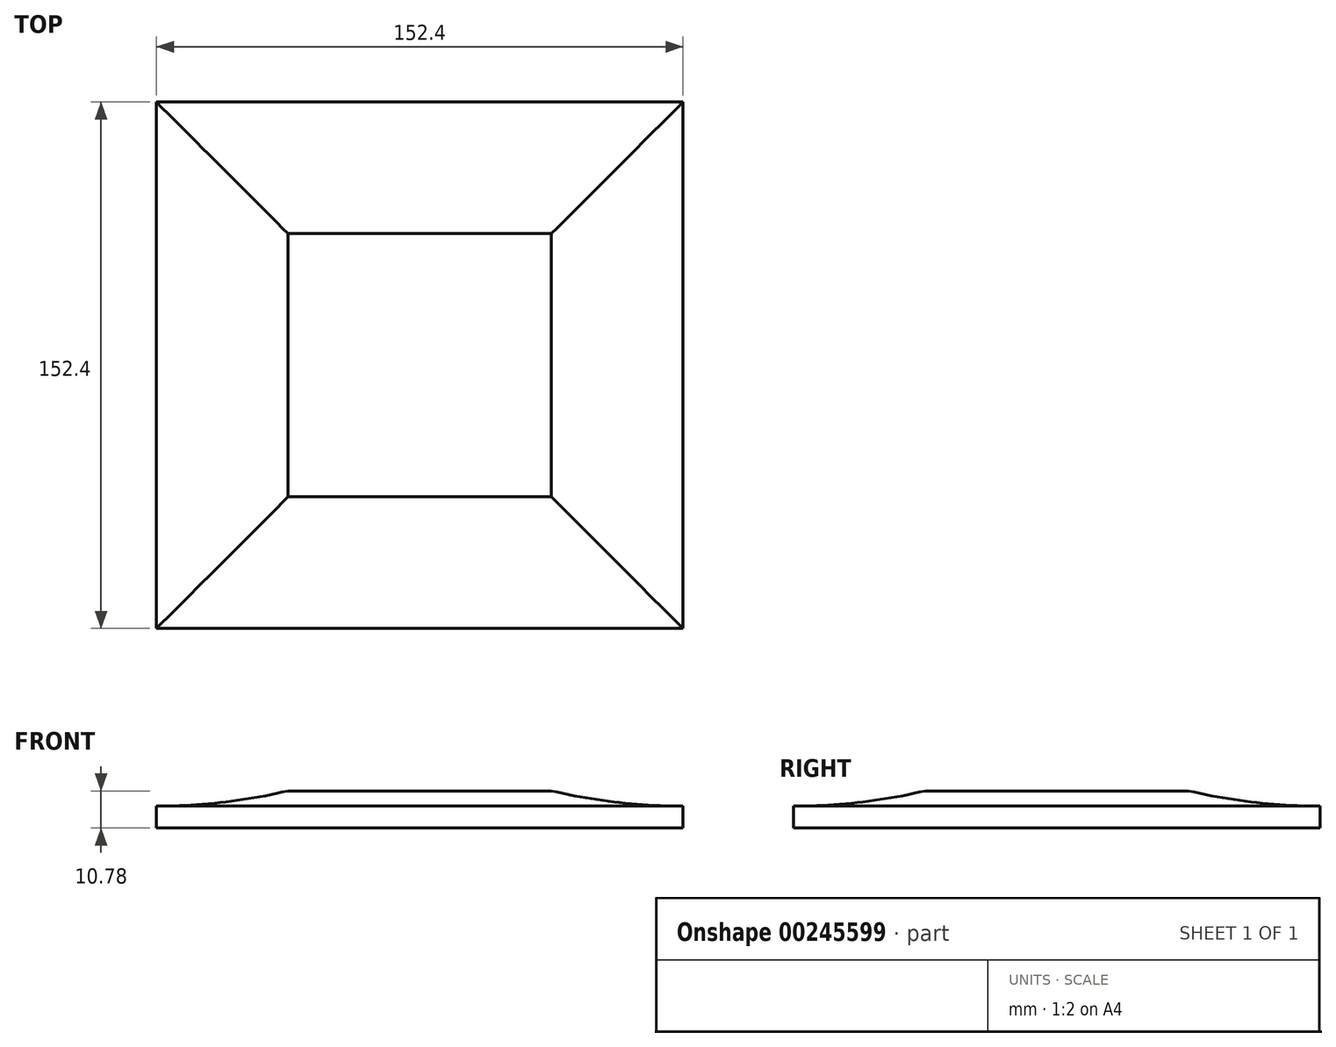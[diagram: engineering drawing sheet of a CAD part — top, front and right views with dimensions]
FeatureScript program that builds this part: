
annotation { "Feature Type Name" : "Feature", "Feature Type Description" : "" }
export const myFeature = defineFeature(function(context is Context, id is Id, definition is map)
    precondition{}
    {
        {
            var Q0;
            Q0=qCreatedBy(makeId("Front.planeOp"),FACE);
            var sketch = newSketch(context, id + "F0", { "sketchPlane" : qUnion([Q0])});
            skLineSegment(sketch, "E0", {"start": v(0, 0) * mm, "end": v(76.2, 0) * mm});
            skLineSegment(sketch, "E1", {"start": v(76.2, 0) * mm, "end": v(76.2, 6.35) * mm});
            skLineSegment(sketch, "E2", {"start": v(38.1, 10.78) * mm, "end": v(0, 10.78) * mm});
            skLineSegment(sketch, "E3", {"start": v(0, 10.78) * mm, "end": v(0, 0) * mm});
            skLineSegment(sketch, "E4", {"start": v(76.2, 6.35) * mm, "end": v(131.75, 6.35) * mm, "construction": true});
            skArc(sketch, "E5", {"start": v(76.2, 6.35) * mm, "mid": v(57.02, 7.46) * mm, "end": v(38.1, 10.78) * mm});
            skSolve(sketch);
        }
        {
            var Q0;
            Q0=qCreatedBy(makeId("Top.planeOp"),FACE);
            var sketch = newSketch(context, id + "F1", { "sketchPlane" : qUnion([Q0])});
            skLineSegment(sketch, "E6.bottom", {"start": v(-76.2, 76.2) * mm, "end": v(76.2, 76.2) * mm});
            skLineSegment(sketch, "E6.top", {"start": v(-76.2, -76.2) * mm, "end": v(76.2, -76.2) * mm});
            skLineSegment(sketch, "E6.left", {"start": v(-76.2, 76.2) * mm, "end": v(-76.2, -76.2) * mm});
            skLineSegment(sketch, "E6.right", {"start": v(76.2, 76.2) * mm, "end": v(76.2, -76.2) * mm});
            skPoint(sketch, "E6.middle", {"position": v(0, 0) * mm});
            skSolve(sketch);
        }
        {
            var Q0;
            Q0=makeQuery(id+"F0.imprint","IMPRINT",FACE,{"disambiguationData":[TD([[makeQuery(id+"F0.imprint","IMPRINT",EDGE,{"derivedFrom":sQuery(id+"F0.wireOp",EDGE,"E0")}),1.0]])]});
            var Q1;
            Q1=sQuery(id+"F1.wireOp",EDGE,"E6.right");
            var Q2;
            Q2=sQuery(id+"F1.wireOp",EDGE,"E6.bottom");
            var Q3;
            Q3=sQuery(id+"F1.wireOp",EDGE,"E6.left");
            var Q4;
            Q4=sQuery(id+"F1.wireOp",EDGE,"E6.top");
            sweep(context, id + "F2", {"profiles" : qUnion([Q0]), "path" : qUnion([Q1, Q2, Q3, Q4])});
        }
    });
